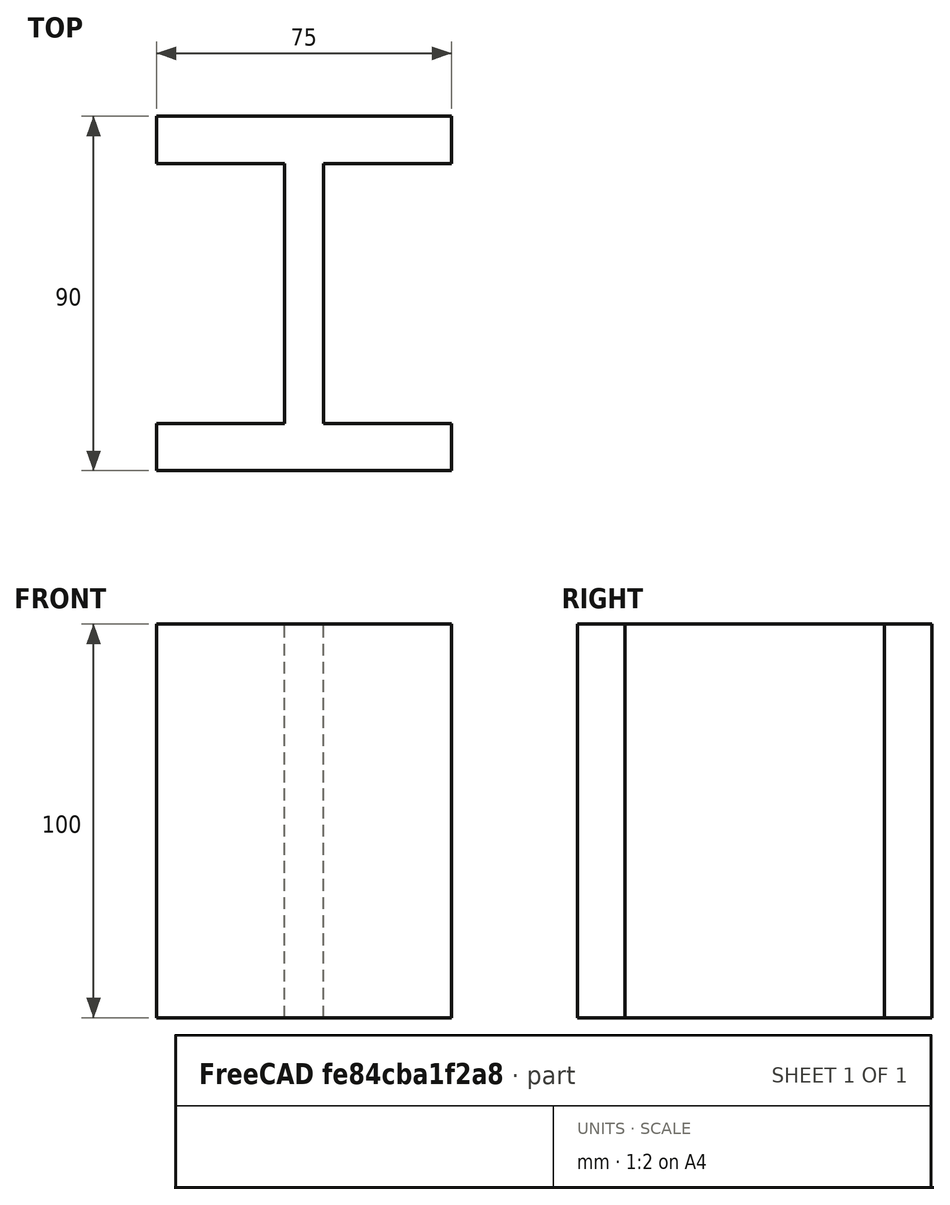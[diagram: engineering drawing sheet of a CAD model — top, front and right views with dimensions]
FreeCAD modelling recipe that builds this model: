
FCSTD DOCUMENT  (FreeCAD 0.16R6707 (Git))
Label: Viga_h
License: CreativeCommons Attribution-ShareAlike
LicenseURL: http://creativecommons.org/licenses/by-sa/4.0/
objects: Sketcher::SketchObject×1, PartDesign::Pad×1
note: 3 computed .brp shape members not serialized (recipe doc carries the construction recipe); baked Part::Feature solids carry a one-line shape summary decoded from their .brp

FEATURE [Sketcher::SketchObject] Sketch  label="Boceto_H"
  sketch-geometry (12):
    g0: LineSegment StartX=-37.5 StartY=45 StartZ=0 EndX=37.5 EndY=45 EndZ=0
    g1: LineSegment StartX=37.5 StartY=45 StartZ=0 EndX=37.5 EndY=33 EndZ=0
    g2: LineSegment StartX=37.5 StartY=33 StartZ=0 EndX=5 EndY=33 EndZ=0
    g3: LineSegment StartX=5 StartY=33 StartZ=0 EndX=5 EndY=-33 EndZ=0
    g4: LineSegment StartX=5 StartY=-33 StartZ=0 EndX=37.5 EndY=-33 EndZ=0
    g5: LineSegment StartX=37.5 StartY=-33 StartZ=0 EndX=37.5 EndY=-45 EndZ=0
    g6: LineSegment StartX=37.5 StartY=-45 StartZ=0 EndX=-37.5 EndY=-45 EndZ=0
    g7: LineSegment StartX=-37.5 StartY=-45 StartZ=0 EndX=-37.5 EndY=-33 EndZ=0
    g8: LineSegment StartX=-37.5 StartY=-33 StartZ=0 EndX=-5 EndY=-33 EndZ=0
    g9: LineSegment StartX=-5 StartY=-33 StartZ=0 EndX=-5 EndY=33 EndZ=0
    g10: LineSegment StartX=-5 StartY=33 StartZ=0 EndX=-37.5 EndY=33 EndZ=0
    g11: LineSegment StartX=-37.5 StartY=33 StartZ=0 EndX=-37.5 EndY=45 EndZ=0
  constraints (34):
    c: Horizontal(g0)
    c: Coincident(g0,g1)
    c: Coincident(g1,g2)
    c: Horizontal(g2)
    c: Coincident(g2,g3)
    c: Vertical(g3)
    c: Coincident(g3,g4)
    c: Horizontal(g4)
    c: Coincident(g4,g5)
    c: Coincident(g5,g6)
    c: Coincident(g6,g7)
    c: Vertical(g7)
    c: Coincident(g7,g8)
    c: Horizontal(g8)
    c: Coincident(g8,g9)
    c: Coincident(g9,g10)
    c: Horizontal(g10)
    c: Coincident(g10,g11)
    c: Coincident(g0,g11)
    c: DistanceX(g0,g0) = 75
    c: Equal(g0,g6)
    c: Symmetric(g6,g5,g-2)
    c: Symmetric(g0,g0,g-2)
    c: Parallel(g9,g3)
    c: Symmetric(g9,g2,g-2)
    c: DistanceX(g8,g3) = 10
    c: DistanceY(g10,g0) = 12
    c: Parallel(g11,g1)
    c: Perpendicular(g0,g11)
    c: Perpendicular(g6,g5)
    c: DistanceY(g5,g0) = 90
    c: DistanceY(g5,g4) = 12
    c: Equal(g5,g7)
    c: Symmetric(g0,g6,g-1)
FEATURE [PartDesign::Pad] Pad  label="Viga"
  Length = 100
  Length2 = 100
  Sketch = -> Sketch
  Type = 0
